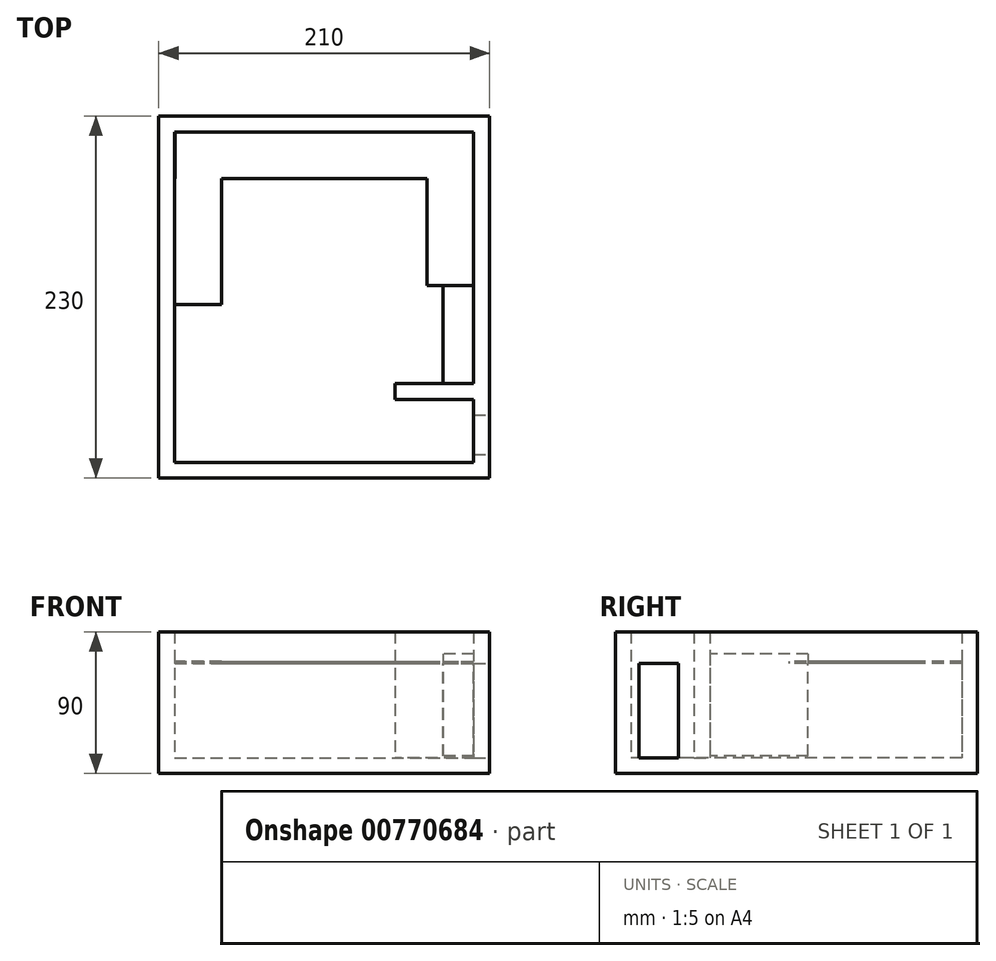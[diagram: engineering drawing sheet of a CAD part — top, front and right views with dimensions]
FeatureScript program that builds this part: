
annotation { "Feature Type Name" : "Feature", "Feature Type Description" : "" }
export const myFeature = defineFeature(function(context is Context, id is Id, definition is map)
    precondition{}
    {
        {
            var Q0;
            Q0=qCreatedBy(makeId("Top.planeOp"),FACE);
            var sketch = newSketch(context, id + "F0", { "sketchPlane" : qUnion([Q0])});
            skLineSegment(sketch, "E0.bottom", {"start": v(-104.52, 150.3) * mm, "end": v(85.48, 150.3) * mm});
            skLineSegment(sketch, "E0.top", {"start": v(-104.52, -59.7) * mm, "end": v(85.48, -59.7) * mm});
            skLineSegment(sketch, "E0.left", {"start": v(-104.52, 150.3) * mm, "end": v(-104.52, -59.7) * mm});
            skLineSegment(sketch, "E0.right", {"start": v(85.48, 150.3) * mm, "end": v(85.48, -59.7) * mm});
            skLineSegment(sketch, "E1.bottom", {"start": v(35.48, -59.7) * mm, "end": v(85.48, -59.7) * mm});
            skLineSegment(sketch, "E1.top", {"start": v(35.48, -19.7) * mm, "end": v(85.48, -19.7) * mm});
            skLineSegment(sketch, "E1.left", {"start": v(35.48, -59.7) * mm, "end": v(35.48, -19.7) * mm});
            skLineSegment(sketch, "E1.right", {"start": v(85.48, -59.7) * mm, "end": v(85.48, -19.7) * mm});
            skLineSegment(sketch, "E2.bottom", {"start": v(-114.52, 160.3) * mm, "end": v(95.48, 160.3) * mm});
            skLineSegment(sketch, "E2.top", {"start": v(-114.52, -69.7) * mm, "end": v(95.48, -69.7) * mm});
            skLineSegment(sketch, "E2.left", {"start": v(-114.52, 160.3) * mm, "end": v(-114.52, -69.7) * mm});
            skLineSegment(sketch, "E2.right", {"start": v(95.48, 160.3) * mm, "end": v(95.48, -69.7) * mm});
            skLineSegment(sketch, "E3", {"start": v(85.48, -9.7) * mm, "end": v(35.48, -9.7) * mm});
            skLineSegment(sketch, "E4", {"start": v(35.48, -19.7) * mm, "end": v(35.48, -9.7) * mm});
            skSolve(sketch);
        }
        {
            var Q0;
            {var subQ3=sQuery(id+"F0.wireOp",EDGE,"E0.bottom");Q0=makeQuery(id+"F0.imprint","IMPRINT",FACE,{"disambiguationData":[TD([[makeQuery(id+"F0.imprint","IMPRINT",EDGE,{"derivedFrom":subQ3}),1.0]])]});}
            var Q1;
            {var subQ0=sQuery(id+"F0.wireOp",EDGE,"E1.top");Q1=makeQuery(id+"F0.imprint","IMPRINT",FACE,{"disambiguationData":[TD([[makeQuery(id+"F0.imprint","IMPRINT",EDGE,{"derivedFrom":subQ0}),1.0]])]});}
            extrude(context, id + "F1", {"entities" : qUnion([Q0, Q1]), "depth" : 80 * mm, "offsetDistance" : 25 * mm});
        }
        {
            var Q0;
            Q0=makeQuery(id+"F1.opExtrude","CAP_FACE",FACE,{"disambiguationData":[OSD([sQuery(id+"F0.wireOp",EDGE,"E0.bottom"),sQuery(id+"F0.wireOp",EDGE,"E0.top"),sQuery(id+"F0.wireOp",EDGE,"E0.left"),sQuery(id+"F0.wireOp",EDGE,"E0.right"),sQuery(id+"F0.wireOp",EDGE,"E1.bottom"),sQuery(id+"F0.wireOp",EDGE,"E1.top"),sQuery(id+"F0.wireOp",EDGE,"E1.right"),sQuery(id+"F0.wireOp",EDGE,"E2.bottom"),sQuery(id+"F0.wireOp",EDGE,"E2.top"),sQuery(id+"F0.wireOp",EDGE,"E2.left"),sQuery(id+"F0.wireOp",EDGE,"E2.right"),sQuery(id+"F0.wireOp",EDGE,"E3"),sQuery(id+"F0.wireOp",EDGE,"E4")])],"isStart":true});
            var sketch = newSketch(context, id + "F2", { "sketchPlane" : qUnion([Q0])});
            skLineSegment(sketch, "E5.bottom", {"start": v(-114.52, 69.7) * mm, "end": v(95.48, 69.7) * mm});
            skLineSegment(sketch, "E5.top", {"start": v(-114.52, -160.3) * mm, "end": v(95.48, -160.3) * mm});
            skLineSegment(sketch, "E5.left", {"start": v(-114.52, 69.7) * mm, "end": v(-114.52, -160.3) * mm});
            skLineSegment(sketch, "E5.right", {"start": v(95.48, 69.7) * mm, "end": v(95.48, -160.3) * mm});
            skSolve(sketch);
        }
        {
            var Q0;
            Q0=makeQuery(id+"F2.imprint","IMPRINT",FACE,{"disambiguationData":[TD([[makeQuery(id+"F2.imprint","IMPRINT",EDGE,{"derivedFrom":makeQuery(id+"F1.opExtrude","CAP_EDGE",EDGE,{"disambiguationData":[OSD([sQuery(id+"F0.wireOp",EDGE,"E0.bottom")])],"isStart":true})}),1.0]])]});
            var Q1;
            Q1=makeQuery(id+"F2.imprint","IMPRINT",FACE,{"disambiguationData":[TD([[makeQuery(id+"F2.imprint","IMPRINT",EDGE,{"derivedFrom":sQuery(id+"F2.wireOp",EDGE,"E5.bottom")}),-1.0]])]});
            extrude(context, id + "F3", {"entities" : qUnion([Q0, Q1]), "operationType" : NewBodyOperationType.ADD, "depth" : 10 * mm, "offsetDistance" : 25 * mm});
        }
        {
            var Q0;
            Q0=makeQuery(id+"F3.opExtrude","CAP_FACE",FACE,{"disambiguationData":[OSD([sQuery(id+"F2.wireOp",EDGE,"E5.bottom"),sQuery(id+"F2.wireOp",EDGE,"E5.top"),sQuery(id+"F2.wireOp",EDGE,"E5.left"),sQuery(id+"F2.wireOp",EDGE,"E5.right")])],"isStart":true});
            cPlane(context, id + "F4", {"entities" : qUnion([Q0]), "cplaneType" : CPlaneType.OFFSET, "offset" : 60 * mm, "width" : 150 * mm, "height" : 150 * mm});
        }
        {
            var Q0;
            Q0=qCreatedBy(id+"F4.planeOp",FACE);
            var sketch = newSketch(context, id + "F5", { "sketchPlane" : qUnion([Q0])});
            skLineSegment(sketch, "E6.bottom", {"start": v(-104.34, 150.5) * mm, "end": v(85.66, 150.5) * mm});
            skLineSegment(sketch, "E6.top", {"start": v(-104.34, 120.5) * mm, "end": v(85.66, 120.5) * mm});
            skLineSegment(sketch, "E6.left", {"start": v(-104.34, 150.5) * mm, "end": v(-104.34, 120.5) * mm});
            skLineSegment(sketch, "E6.right", {"start": v(85.66, 150.5) * mm, "end": v(85.66, 120.5) * mm});
            skLineSegment(sketch, "E7.bottom", {"start": v(85.87, -10.29) * mm, "end": v(65.87, -10.29) * mm});
            skLineSegment(sketch, "E7.top", {"start": v(85.87, 52.71) * mm, "end": v(65.87, 52.71) * mm});
            skLineSegment(sketch, "E7.left", {"start": v(85.87, -10.29) * mm, "end": v(85.87, 52.71) * mm});
            skLineSegment(sketch, "E7.right", {"start": v(65.87, -10.29) * mm, "end": v(65.87, 52.71) * mm});
            skLineSegment(sketch, "E8.bottom", {"start": v(55.87, 120.5) * mm, "end": v(85.87, 120.5) * mm});
            skLineSegment(sketch, "E8.top", {"start": v(55.87, 52.71) * mm, "end": v(85.87, 52.71) * mm});
            skLineSegment(sketch, "E8.left", {"start": v(55.87, 120.5) * mm, "end": v(55.87, 52.71) * mm});
            skLineSegment(sketch, "E8.right", {"start": v(85.87, 120.5) * mm, "end": v(85.87, 52.71) * mm});
            skLineSegment(sketch, "E9.bottom", {"start": v(-74.7, 120.5) * mm, "end": v(-104.7, 120.5) * mm});
            skLineSegment(sketch, "E9.top", {"start": v(-74.7, 40.5) * mm, "end": v(-104.7, 40.5) * mm});
            skLineSegment(sketch, "E9.left", {"start": v(-74.7, 120.5) * mm, "end": v(-74.7, 40.5) * mm});
            skLineSegment(sketch, "E9.right", {"start": v(-104.7, 120.5) * mm, "end": v(-104.7, 40.5) * mm});
            skSolve(sketch);
        }
        {
            var Q0;
            Q0=makeQuery(id+"F5.imprint","IMPRINT",FACE,{"disambiguationData":[TD([[makeQuery(id+"F5.imprint","IMPRINT",EDGE,{"derivedFrom":sQuery(id+"F5.wireOp",EDGE,"E6.bottom")}),-1.0]])]});
            var Q1;
            Q1=makeQuery(id+"F5.imprint","IMPRINT",FACE,{"disambiguationData":[TD([[makeQuery(id+"F5.imprint","IMPRINT",EDGE,{"derivedFrom":sQuery(id+"F5.wireOp",EDGE,"E9.top")}),-1.0]])]});
            var Q2;
            {var subQ3=sQuery(id+"F5.wireOp",EDGE,"E8.left");Q2=makeQuery(id+"F5.imprint","IMPRINT",FACE,{"disambiguationData":[TD([[makeQuery(id+"F5.imprint","IMPRINT",EDGE,{"derivedFrom":subQ3}),1.0]])]});}
            var Q3;
            Q3=makeQuery(id+"F5.imprint","IMPRINT",FACE,{"disambiguationData":[TD([[makeQuery(id+"F5.imprint","IMPRINT",EDGE,{"derivedFrom":sQuery(id+"F5.wireOp",EDGE,"E7.bottom")}),-1.0]])]});
            extrude(context, id + "F6", {"entities" : qUnion([Q0, Q1, Q2, Q3]), "operationType" : NewBodyOperationType.ADD, "depth" : 1 * mm, "offsetDistance" : 25 * mm});
        }
        {
            var Q0;
            Q0=makeQuery(id+"F6.opExtrude","CAP_FACE",FACE,{"disambiguationData":[OSD([sQuery(id+"F5.wireOp",EDGE,"E6.bottom"),sQuery(id+"F5.wireOp",EDGE,"E6.top"),sQuery(id+"F5.wireOp",EDGE,"E6.left"),sQuery(id+"F5.wireOp",EDGE,"E6.right"),sQuery(id+"F5.wireOp",EDGE,"E7.bottom"),sQuery(id+"F5.wireOp",EDGE,"E7.left"),sQuery(id+"F5.wireOp",EDGE,"E7.right"),sQuery(id+"F5.wireOp",EDGE,"E8.bottom"),sQuery(id+"F5.wireOp",EDGE,"E8.top"),sQuery(id+"F5.wireOp",EDGE,"E8.left"),sQuery(id+"F5.wireOp",EDGE,"E8.right"),sQuery(id+"F5.wireOp",EDGE,"E9.bottom"),sQuery(id+"F5.wireOp",EDGE,"E9.top"),sQuery(id+"F5.wireOp",EDGE,"E9.left"),sQuery(id+"F5.wireOp",EDGE,"E9.right")])],"isStart":false});
            var sketch = newSketch(context, id + "F7", { "sketchPlane" : qUnion([Q0])});
            skLineSegment(sketch, "E10.bottom", {"start": v(65.87, 52.71) * mm, "end": v(85.48, 52.71) * mm});
            skLineSegment(sketch, "E10.top", {"start": v(65.87, -9.7) * mm, "end": v(85.48, -9.7) * mm});
            skLineSegment(sketch, "E10.left", {"start": v(65.87, 52.71) * mm, "end": v(65.87, -9.7) * mm});
            skLineSegment(sketch, "E10.right", {"start": v(85.48, 52.71) * mm, "end": v(85.48, -9.7) * mm});
            skSolve(sketch);
        }
        {
            var Q0;
            Q0=makeQuery(id+"F7.imprint","IMPRINT",FACE,{"disambiguationData":[TD([[makeQuery(id+"F7.imprint","IMPRINT",EDGE,{"derivedFrom":sQuery(id+"F7.wireOp",EDGE,"E10.bottom")}),-1.0]])]});
            extrude(context, id + "F8", {"entities" : qUnion([Q0]), "operationType" : NewBodyOperationType.ADD, "oppositeDirection" : true, "depth" : 60 * mm, "offsetDistance" : 25 * mm});
        }
        {
            var Q0;
            Q0=makeQuery(id+"F3.boolean.opBoolean","MERGE",FACE,{"derivedFrom":[makeQuery(id+"F1.opExtrude","SWEPT_FACE",FACE,{"disambiguationData":[OSD([sQuery(id+"F0.wireOp",EDGE,"E2.right")])]}),makeQuery(id+"F3.opExtrude","SWEPT_FACE",FACE,{"disambiguationData":[OSD([sQuery(id+"F2.wireOp",EDGE,"E5.right")])]})]});
            var sketch = newSketch(context, id + "F9", { "sketchPlane" : qUnion([Q0])});
            skLineSegment(sketch, "E11.bottom", {"start": v(-54.7, 0) * mm, "end": v(-29.7, 0) * mm});
            skLineSegment(sketch, "E11.top", {"start": v(-54.7, 60) * mm, "end": v(-29.7, 60) * mm});
            skLineSegment(sketch, "E11.left", {"start": v(-54.7, 0) * mm, "end": v(-54.7, 60) * mm});
            skLineSegment(sketch, "E11.right", {"start": v(-29.7, 0) * mm, "end": v(-29.7, 60) * mm});
            skSolve(sketch);
        }
        {
            var Q0;
            Q0=makeQuery(id+"F9.imprint","IMPRINT",FACE,{"disambiguationData":[TD([[makeQuery(id+"F9.imprint","IMPRINT",EDGE,{"derivedFrom":sQuery(id+"F9.wireOp",EDGE,"E11.bottom")}),1.0]])]});
            extrude(context, id + "F10", {"entities" : qUnion([Q0]), "operationType" : NewBodyOperationType.REMOVE, "endBound" : BoundingType.UP_TO_NEXT, "oppositeDirection" : true, "depth" : 25 * mm, "offsetDistance" : 25 * mm});
        }
        {
            var Q0;
            Q0=makeQuery(id+"F6.opExtrude","CAP_FACE",FACE,{"disambiguationData":[OSD([sQuery(id+"F5.wireOp",EDGE,"E6.bottom"),sQuery(id+"F5.wireOp",EDGE,"E6.top"),sQuery(id+"F5.wireOp",EDGE,"E6.left"),sQuery(id+"F5.wireOp",EDGE,"E6.right"),sQuery(id+"F5.wireOp",EDGE,"E7.bottom"),sQuery(id+"F5.wireOp",EDGE,"E7.left"),sQuery(id+"F5.wireOp",EDGE,"E7.right"),sQuery(id+"F5.wireOp",EDGE,"E8.bottom"),sQuery(id+"F5.wireOp",EDGE,"E8.top"),sQuery(id+"F5.wireOp",EDGE,"E8.left"),sQuery(id+"F5.wireOp",EDGE,"E8.right"),sQuery(id+"F5.wireOp",EDGE,"E9.bottom"),sQuery(id+"F5.wireOp",EDGE,"E9.top"),sQuery(id+"F5.wireOp",EDGE,"E9.left"),sQuery(id+"F5.wireOp",EDGE,"E9.right")])],"isStart":false});
            var sketch = newSketch(context, id + "F11", { "sketchPlane" : qUnion([Q0])});
            skLineSegment(sketch, "E12.bottom", {"start": v(65.87, 52.71) * mm, "end": v(85.48, 52.71) * mm});
            skLineSegment(sketch, "E12.top", {"start": v(65.87, 0) * mm, "end": v(85.48, 0) * mm});
            skLineSegment(sketch, "E12.left", {"start": v(65.87, 52.71) * mm, "end": v(65.87, 0) * mm});
            skLineSegment(sketch, "E12.right", {"start": v(85.48, 52.71) * mm, "end": v(85.48, 0) * mm});
            skSolve(sketch);
        }
        {
            var Q0;
            Q0=makeQuery(id+"F11.imprint","IMPRINT",FACE,{"disambiguationData":[TD([[makeQuery(id+"F11.imprint","IMPRINT",EDGE,{"derivedFrom":sQuery(id+"F11.wireOp",EDGE,"E12.bottom")}),-1.0]])]});
            extrude(context, id + "F12", {"entities" : qUnion([Q0]), "operationType" : NewBodyOperationType.ADD, "depth" : 5 * mm, "offsetDistance" : 25 * mm});
        }
        {
            var Q0;
            {var subQ0=sQuery(id+"F5.wireOp",EDGE,"E7.right");Q0=makeQuery(id+"F12.boolean.opBoolean","SPLIT",FACE,{"disambiguationData":[TD([makeQuery(id+"F1.opExtrude","SWEPT_FACE",FACE,{"disambiguationData":[OSD([sQuery(id+"F0.wireOp",EDGE,"E3")])]})])],"derivedFrom":makeQuery(id+"F6.opExtrude","CAP_FACE",FACE,{"disambiguationData":[OSD([sQuery(id+"F5.wireOp",EDGE,"E6.bottom"),sQuery(id+"F5.wireOp",EDGE,"E6.top"),sQuery(id+"F5.wireOp",EDGE,"E6.left"),sQuery(id+"F5.wireOp",EDGE,"E6.right"),sQuery(id+"F5.wireOp",EDGE,"E7.bottom"),sQuery(id+"F5.wireOp",EDGE,"E7.left"),subQ0,sQuery(id+"F5.wireOp",EDGE,"E8.bottom"),sQuery(id+"F5.wireOp",EDGE,"E8.top"),sQuery(id+"F5.wireOp",EDGE,"E8.left"),sQuery(id+"F5.wireOp",EDGE,"E8.right"),sQuery(id+"F5.wireOp",EDGE,"E9.bottom"),sQuery(id+"F5.wireOp",EDGE,"E9.top"),sQuery(id+"F5.wireOp",EDGE,"E9.left"),sQuery(id+"F5.wireOp",EDGE,"E9.right")])],"isStart":false})});}
            extrude(context, id + "F13", {"entities" : qUnion([Q0]), "operationType" : NewBodyOperationType.ADD, "depth" : 5 * mm, "offsetDistance" : 25 * mm});
        }
    });
